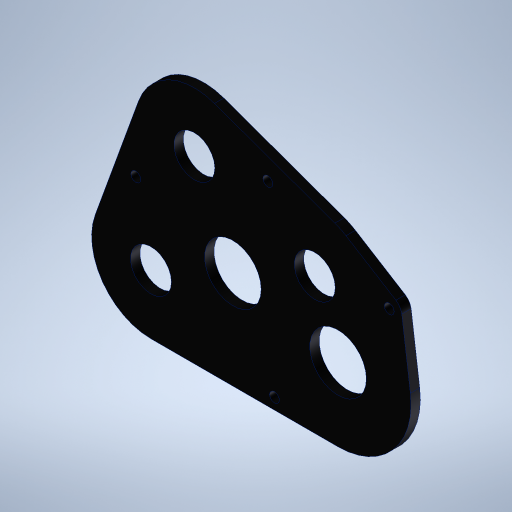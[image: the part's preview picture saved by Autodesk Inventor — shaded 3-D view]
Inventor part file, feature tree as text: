
AUTODESK INVENTOR PART (.ipt)
format: ipt  version: 2024 (Build 280153000, 153)  size: 292,352 bytes
history: native  units: in
note: dims shown in document units (in); Inventor stores cm internally (conversion verified against a paired STEP export)
features: extrude x1, sketch x1
ambient origin geometry x8: Origin, YZ Plane, XZ Plane, XY Plane, X Axis, Y Axis, Z Axis, Center Point
bodies: Solid1 (feature_tree)
feature tree (2):
  extrude  "Extrusion1"  Depth=0.1875in
  sketch  "Sketch1"  dims[d0=3.0in d1=0.6in d2=2.36in d3=1.5in d4=2.8in d5=1.125in d6=0.813in d8=0.375in d9=2.9in d10=0.1in d12=0.5in d13=0.196in d14=0.0625in d15=0.5in d16=0.196in d17=0.5in d18=0.196in d19=0.5in d20=0.196in d21=0.0625in d22=0.0625in d23=0.0625in d24=0.0625in d25=0.1875in d26=0.0in]
